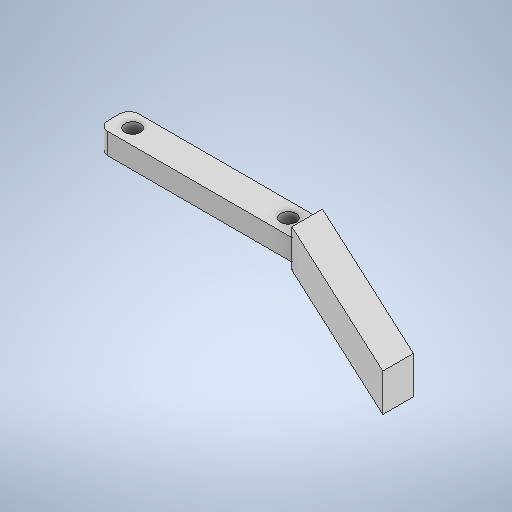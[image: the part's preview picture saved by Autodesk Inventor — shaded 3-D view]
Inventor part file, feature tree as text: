
AUTODESK INVENTOR PART (.ipt)
format: ipt  version: 2025.1 (Build 291241020, 241B)  size: 755,712 bytes
history: native  units: in
note: dims shown in document units (in); Inventor stores cm internally (conversion verified against a paired STEP export)
features: extrude x17, sketch x17, other x3, fillet x3, pattern_circular x1
ambient origin geometry x8: Origin, YZ Plane, XZ Plane, XY Plane, X Axis, Y Axis, Z Axis, Center Point
bodies: Solid1 (feature_tree)
feature tree (41):
  other  "servoMoldAssembly.iam"
  other  "block.ipt:1"
  other  "sg90horn.ipt:1"
  extrude  "Extrusion1"  Depth=0.3937in TaperAngle=0.0deg
  extrude  "Extrusion2"  Depth=0.3937in TaperAngle=0.0deg
  extrude  "Extrusion3"  Depth=0.0591in TaperAngle=0.0deg
  extrude  "Extrusion4"  Depth=0.0591in TaperAngle=0.0deg
  extrude  "Extrusion5"  Depth=1.9685in
  extrude  "Extrusion6"  Depth=0.3937in TaperAngle=0.0deg
  extrude  "Extrusion7"  Depth=0.2362in TaperAngle=0.0deg
  extrude  "Extrusion8"  Depth=0.2362in
  extrude  "Extrusion10"  Depth=0.2362in TaperAngle=0.0deg
  extrude  "Extrusion11"  Depth=0.2362in TaperAngle=0.0deg
  fillet  "Fillet1"  Radius=0.0787in
  extrude  "Extrusion12"  Depth=0.8268in
  fillet  "Fillet2"  Radius=1.1934in
  extrude  "Extrusion13"  TaperAngle=90.0deg  [1 undecoded]
  pattern_circular  "Circular Pattern2"  Count=20 Angle=240.0deg
  extrude  "Extrusion14"  Depth=0.3937in
  extrude  "Extrusion15"  Depth=0.3937in
  extrude  "Extrusion16"  Depth=0.0787in
  fillet  "Fillet3"  Radius=1.3032in
  extrude  "Extrusion17"  Depth=0.2362in
  extrude  "Extrusion18"  Depth=0.2362in
  sketch  "Sketch3"  dims[d0=0.3937in d1=0.3937in d2=0.0in]
  sketch  "Sketch4"  dims[d3=0.2795in d4=0.3937in d5=0.0in]
  sketch  "Sketch5"  dims[d6=0.0591in d7=0.0in d8=0.0591in d9=0.0in]
  sketch  "Sketch6"  dims[d10=0.0591in d11=0.0in d12=0.0591in d13=0.0in]
  sketch  "Sketch7"  dims[d14=1.4173in d15=1.9685in]
  sketch  "Sketch8"  dims[d16=0.0in d17=0.3937in d18=0.0in]
  sketch  "Sketch9"  dims[d19=0.3937in d20=0.0in d29=0.2362in d30=0.0in]
  sketch  "Sketch10"  dims[d31=0.2362in d32=0.1299in]
  sketch  "Sketch12"  dims[d33=0.0787in d34=0.2362in d35=0.0in]
  sketch  "Sketch13"  dims[d36=0.0787in d37=0.2362in d38=0.0in d39=0.0787in]
  sketch  "Sketch14"  dims[d40=0.0984in d41=0.8268in d42=1.1934in]
  sketch  "Sketch15"  dims[d43=0.0591in d44=90.0deg]
  sketch  "Sketch16"  dims[d45=0.3937in d46=0.0in d47=7.874in d48=240.0deg]
  sketch  "Sketch17"  dims[d50=0.3937in d51=0.0in d52=0.1299in]
  sketch  "Sketch18"  dims[d53=0.3937in d54=0.0in d55=0.1575in]
  sketch  "Sketch19"  dims[d56=0.3937in d57=0.0in d58=0.0787in d60=1.3032in]
  sketch  "Sketch20"  dims[d61=0.1299in d62=0.1575in d63=0.0in d64=0.3937in d65=0.0in d66=1.5748in d67=0.1718in d68=1.5748in d69=0.1718in d70=0.0984in d71=0.0787in d72=0.2362in d73=0.0in d74=0.0in]
note: 1 required parameter value undecoded (feature->parameter linkage not recoverable at this tier; creation-order binding heuristic only, values carry confidence <= 0.55)
